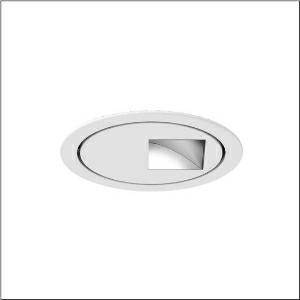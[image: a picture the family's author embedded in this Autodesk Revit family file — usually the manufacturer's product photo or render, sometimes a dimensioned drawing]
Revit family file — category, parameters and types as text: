
# Revit family: lunis_11_mini_round_51dk11cd2wn21
name_source: partatom
category: Lighting Fixtures
units: mm (PartAtom-declared; Revit-internal decimal feet)

## family parameters
Cut with Voids When Loaded = No
Host = Face
Light Source = No
Part Type = Normal
Room Calculation Point = No
Round Connector Dimension = Use Diameter
Shared = No

## types (1)
- Lunis 11 mini round (1 x LED 4000K / CRI = 90 (unbekannt), 2120 lm, 4000K)
    Apparent Load = 28 VA
    CIE Flux Codes = 44 77 97 100 100
    Color Rendering = 90
    Color Temperature = 4000K
    Default Elevation = 1800 mm
    Description = Lunis 11 mini round, downlight, light control with wallwasher, of highly reflective aluminium, highly specular, light emission: direct distribution, LED rated luminous flux: 2.120lm, light colour: 940, control gear: ECG, with terminal, 5-pole, mains connection: 220..230V, AC/DC, 0/50..60Hz, LED module, luminaire module, of aluminium, highly specular, white, diameter: 176mm, clamping range: 1..40mm, recessing ring, of plastic, traffic white (RAL 9016), protection rating (complete): IP20, insulation class (complete): insulation class II (safety insulation), certification: CE, permissible ambient temperature for indoor applications: 0..+35°C, packaging unit: 1 piece
    Height = 0 mm  [stored 0 ft]
    Lamp = 1 x LED 4000K / CRI >= 90 (unbekannt)
    Lamp Light Flux = 2120 lm
    Lamp count = 1
    Length = 176 mm
    Luminous efficacy = 76 lm/W
    Manufacturer = Siteco
    ModVariant = No
    Model = 51DK11CD2WN21
    Mounting Place = Ceiling
    Mounting Type = Recessed
    Number of Poles = 1
    OnlyDefault = Yes
    Power Factor = 1
    Product Name = Lunis 11 mini round
    Product group = downlight
    ProductGroupID = 401
    Protection Class = Protection class II
    Protection Degree = IP 20
    RLX_Detail_Level = 1
    RLX_Emergency_Light_Flux = 0 lm
    RLX_Emergency_Type = 0
    RLX_Emergency_Type_DB = No
    RlxData = <blob elided: 59385 chars, md5=0bd0f8b9>
    Socket = socket
    Standby Power = 0 W
    System Light Flux = 2120 lm
    System Power = 28 W
    Type Comments = Product without accessories
    Type Image = l_1004772.jpg
    URL = http://relux.com
    VarID = ---
    Voltage = 0 V
    Weight = 0.00 kg
    Width = 176 mm

note: [stored X ft] marks values corroborated as IEEE doubles in the binary element streams (Revit-internal decimal feet)

## geometry (parser evidence)
native form markers: Blend x4, Sweep x12
no freeform markers — native parametric forms only
